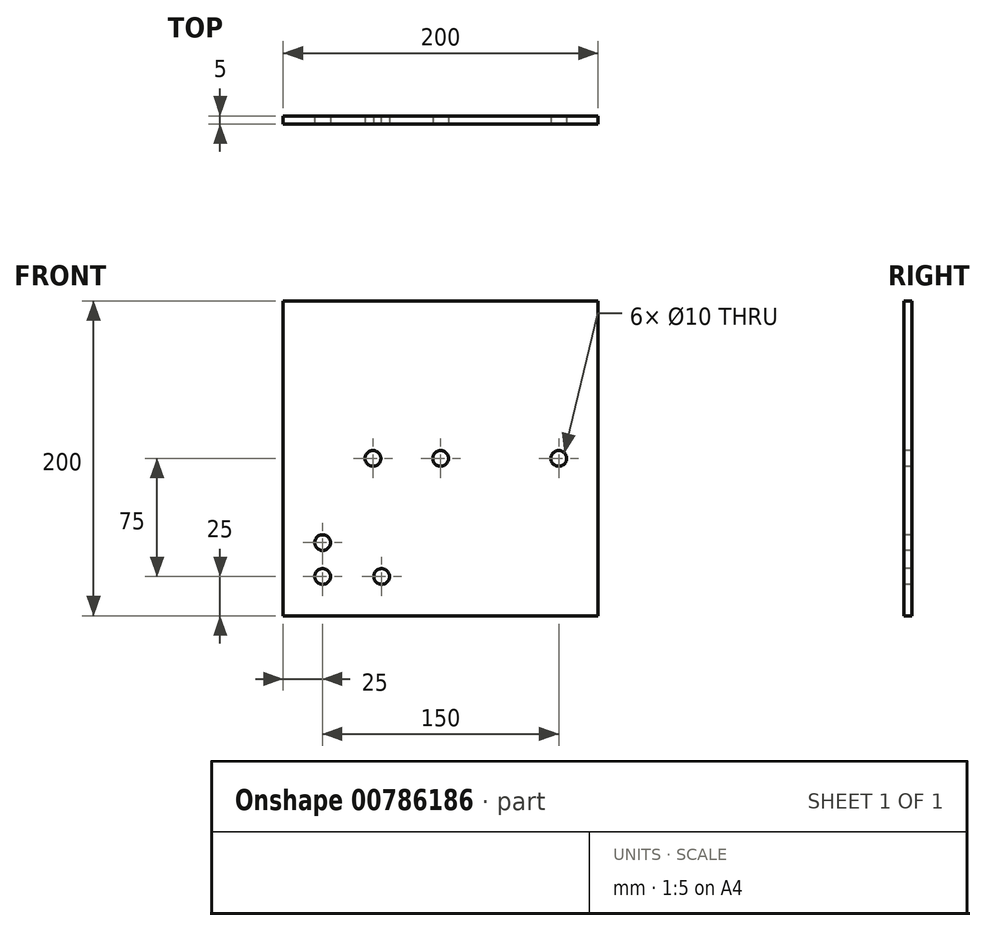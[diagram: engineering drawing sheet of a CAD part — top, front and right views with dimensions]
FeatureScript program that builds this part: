
annotation { "Feature Type Name" : "Feature", "Feature Type Description" : "" }
export const myFeature = defineFeature(function(context is Context, id is Id, definition is map)
    precondition{}
    {
        {
            var Q0;
            Q0=qCreatedBy(makeId("Front.planeOp"),FACE);
            var sketch = newSketch(context, id + "F0", { "sketchPlane" : qUnion([Q0])});
            skLineSegment(sketch, "E0.bottom", {"start": v(-100, 100) * mm, "end": v(100, 100) * mm});
            skLineSegment(sketch, "E0.top", {"start": v(-100, -100) * mm, "end": v(100, -100) * mm});
            skLineSegment(sketch, "E0.left", {"start": v(-100, 100) * mm, "end": v(-100, -100) * mm});
            skLineSegment(sketch, "E0.right", {"start": v(100, 100) * mm, "end": v(100, -100) * mm});
            skCircle(sketch, "E1", {"center": v(-43, 0) * mm, "radius": 5 * mm});
            skCircle(sketch, "E2", {"center": v(0, 0) * mm, "radius": 5 * mm});
            skCircle(sketch, "E3", {"center": v(75, 0) * mm, "radius": 5 * mm});
            skCircle(sketch, "E4", {"center": v(-75, -53.5) * mm, "radius": 5 * mm});
            skCircle(sketch, "E5", {"center": v(-75, -75) * mm, "radius": 5 * mm});
            skCircle(sketch, "E6", {"center": v(-37.5, -75) * mm, "radius": 5 * mm});
            skSolve(sketch);
        }
        {
            var Q0;
            Q0 = qSketchRegion(id + "F0", true);
            extrude(context, id + "F1", {"entities" : qUnion([Q0]), "oppositeDirection" : true, "depth" : 5 * mm, "offsetDistance" : 25 * mm});
        }
    });
